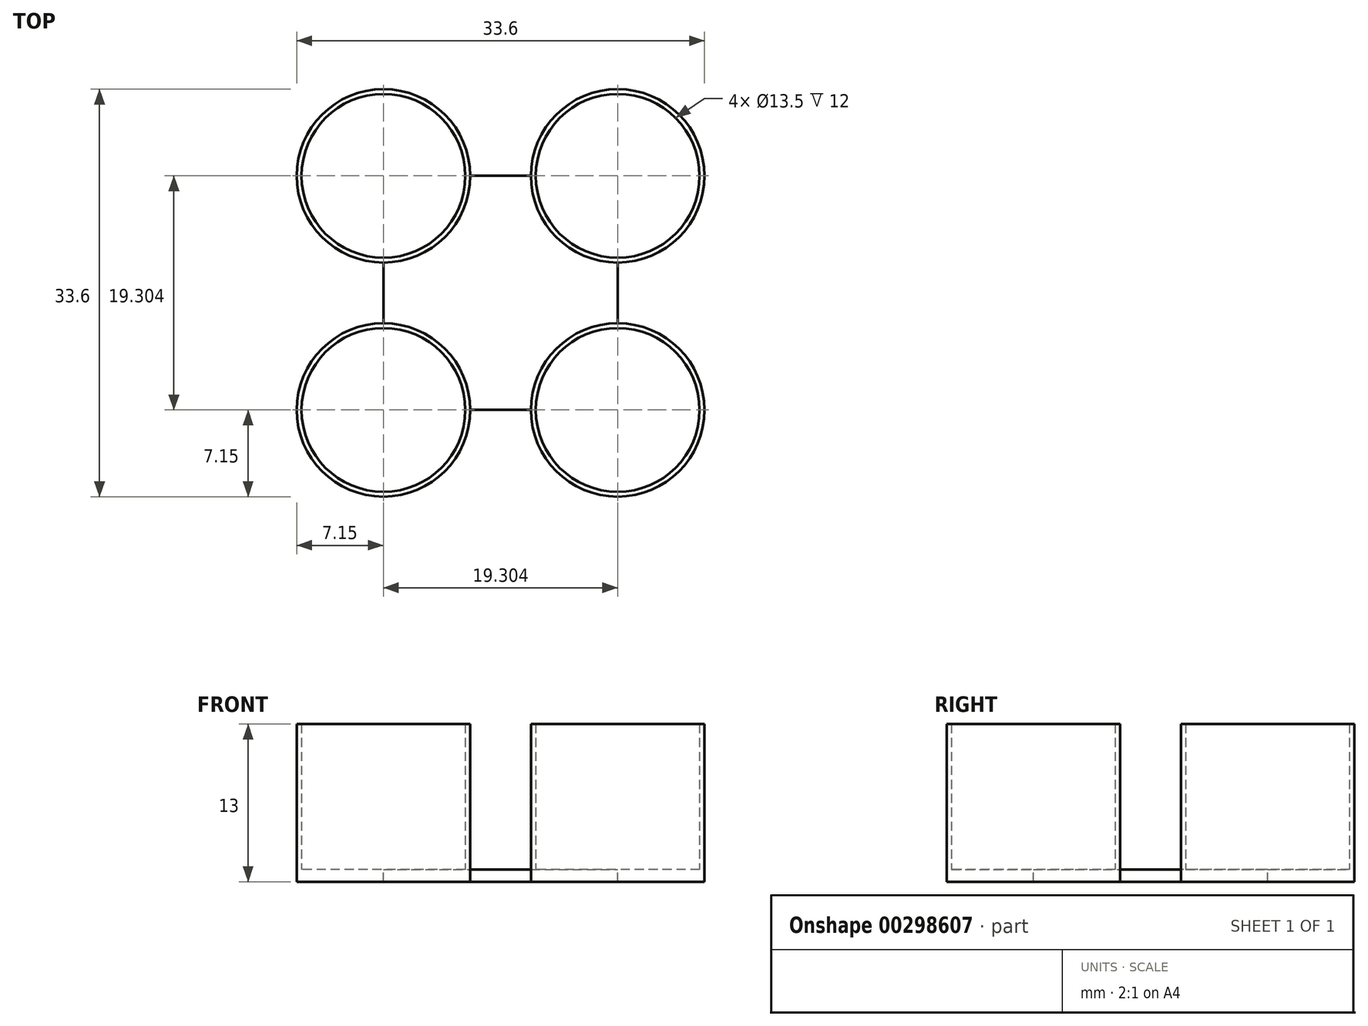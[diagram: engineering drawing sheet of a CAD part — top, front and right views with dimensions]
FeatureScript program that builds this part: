
annotation { "Feature Type Name" : "Feature", "Feature Type Description" : "" }
export const myFeature = defineFeature(function(context is Context, id is Id, definition is map)
    precondition{}
    {
        {
            var Q0;
            Q0=qCreatedBy(makeId("Top.planeOp"),FACE);
            var sketch = newSketch(context, id + "F0", { "sketchPlane" : qUnion([Q0])});
            skCircle(sketch, "E0", {"center": v(0, 0) * mm, "radius": 6.75 * mm});
            skCircle(sketch, "E1", {"center": v(0, 0) * mm, "radius": 7.15 * mm});
            skCircle(sketch, "E2.0.1.0", {"center": v(0, 19.3) * mm, "radius": 7.15 * mm});
            skCircle(sketch, "E2.0.1.1", {"center": v(0, 19.3) * mm, "radius": 6.75 * mm});
            skCircle(sketch, "E2.1.0.0", {"center": v(19.3, 0) * mm, "radius": 7.15 * mm});
            skCircle(sketch, "E2.1.0.1", {"center": v(19.3, 0) * mm, "radius": 6.75 * mm});
            skCircle(sketch, "E2.1.1.0", {"center": v(19.3, 19.3) * mm, "radius": 7.15 * mm});
            skCircle(sketch, "E2.1.1.1", {"center": v(19.3, 19.3) * mm, "radius": 6.75 * mm});
            skLineSegment(sketch, "E2.direction1", {"start": v(0, 0) * mm, "end": v(19.3, 0) * mm, "construction": true});
            skLineSegment(sketch, "E2.direction2", {"start": v(0, 0) * mm, "end": v(0, 19.3) * mm, "construction": true});
            skLineSegment(sketch, "E3", {"start": v(19.3, 19.3) * mm, "end": v(19.3, 0) * mm});
            skLineSegment(sketch, "E4", {"start": v(0, 19.3) * mm, "end": v(0, 0) * mm});
            skLineSegment(sketch, "E5", {"start": v(19.3, 19.3) * mm, "end": v(0, 19.3) * mm});
            skLineSegment(sketch, "E6", {"start": v(19.3, 0) * mm, "end": v(0, 0) * mm});
            skSolve(sketch);
        }
        {
            var Q0;
            {var subQ5=sQuery(id+"F0.wireOp",EDGE,"E4");var subQ13=sQuery(id+"F0.wireOp",EDGE,"E1");var subQ14=makeQuery(id+"F0.imprint","INTERSECT",VERTEX,{"derivedFrom":[subQ13,subQ5]});Q0=makeQuery(id+"F0.imprint","IMPRINT",FACE,{"disambiguationData":[TD([[makeQuery(id+"F0.imprint","IMPRINT",EDGE,{"disambiguationData":[TD([[subQ14,1.0]])],"derivedFrom":subQ13}),-1.0]])]});}
            var Q1;
            {var subQ0=sQuery(id+"F0.wireOp",EDGE,"E4");var subQ1=sQuery(id+"F0.wireOp",EDGE,"E2.0.1.0");var subQ2=makeQuery(id+"F0.imprint","INTERSECT",VERTEX,{"derivedFrom":[subQ1,subQ0]});Q1=makeQuery(id+"F0.imprint","IMPRINT",FACE,{"disambiguationData":[TD([[makeQuery(id+"F0.imprint","IMPRINT",EDGE,{"disambiguationData":[TD([[subQ2,-1.0]])],"derivedFrom":subQ1}),1.0]])]});}
            var Q2;
            {var subQ0=sQuery(id+"F0.wireOp",EDGE,"E3");var subQ1=sQuery(id+"F0.wireOp",EDGE,"E2.1.0.0");var subQ2=makeQuery(id+"F0.imprint","INTERSECT",VERTEX,{"derivedFrom":[subQ1,subQ0]});Q2=makeQuery(id+"F0.imprint","IMPRINT",FACE,{"disambiguationData":[TD([[makeQuery(id+"F0.imprint","IMPRINT",EDGE,{"disambiguationData":[TD([[subQ2,-1.0]])],"derivedFrom":subQ1}),1.0]])]});}
            var Q3;
            {var subQ0=sQuery(id+"F0.wireOp",EDGE,"E4");var subQ1=sQuery(id+"F0.wireOp",EDGE,"E0");var subQ2=makeQuery(id+"F0.imprint","INTERSECT",VERTEX,{"derivedFrom":[subQ1,subQ0]});Q3=makeQuery(id+"F0.imprint","IMPRINT",FACE,{"disambiguationData":[TD([[makeQuery(id+"F0.imprint","IMPRINT",EDGE,{"disambiguationData":[TD([[subQ2,1.0]])],"derivedFrom":subQ1}),1.0]])]});}
            var Q4;
            {var subQ0=sQuery(id+"F0.wireOp",EDGE,"E4");var subQ1=sQuery(id+"F0.wireOp",EDGE,"E0");var subQ2=makeQuery(id+"F0.imprint","INTERSECT",VERTEX,{"derivedFrom":[subQ1,subQ0]});Q4=makeQuery(id+"F0.imprint","IMPRINT",FACE,{"disambiguationData":[TD([[makeQuery(id+"F0.imprint","IMPRINT",EDGE,{"disambiguationData":[TD([[subQ2,-1.0]])],"derivedFrom":subQ1}),-1.0]])]});}
            var Q5;
            {var subQ0=sQuery(id+"F0.wireOp",EDGE,"E4");var subQ1=sQuery(id+"F0.wireOp",EDGE,"E0");var subQ2=makeQuery(id+"F0.imprint","INTERSECT",VERTEX,{"derivedFrom":[subQ1,subQ0]});Q5=makeQuery(id+"F0.imprint","IMPRINT",FACE,{"disambiguationData":[TD([[makeQuery(id+"F0.imprint","IMPRINT",EDGE,{"disambiguationData":[TD([[subQ2,-1.0]])],"derivedFrom":subQ1}),1.0]])]});}
            var Q6;
            {var subQ0=sQuery(id+"F0.wireOp",EDGE,"E4");var subQ1=sQuery(id+"F0.wireOp",EDGE,"E2.0.1.0");var subQ2=makeQuery(id+"F0.imprint","INTERSECT",VERTEX,{"derivedFrom":[subQ1,subQ0]});Q6=makeQuery(id+"F0.imprint","IMPRINT",FACE,{"disambiguationData":[TD([[makeQuery(id+"F0.imprint","IMPRINT",EDGE,{"disambiguationData":[TD([[subQ2,1.0]])],"derivedFrom":subQ1}),1.0]])]});}
            var Q7;
            {var subQ0=sQuery(id+"F0.wireOp",EDGE,"E4");var subQ1=sQuery(id+"F0.wireOp",EDGE,"E2.0.1.1");var subQ2=makeQuery(id+"F0.imprint","INTERSECT",VERTEX,{"derivedFrom":[subQ1,subQ0]});Q7=makeQuery(id+"F0.imprint","IMPRINT",FACE,{"disambiguationData":[TD([[makeQuery(id+"F0.imprint","IMPRINT",EDGE,{"disambiguationData":[TD([[subQ2,1.0]])],"derivedFrom":subQ1}),1.0]])]});}
            var Q8;
            {var subQ0=sQuery(id+"F0.wireOp",EDGE,"E4");var subQ1=sQuery(id+"F0.wireOp",EDGE,"E2.0.1.1");var subQ2=makeQuery(id+"F0.imprint","INTERSECT",VERTEX,{"derivedFrom":[subQ1,subQ0]});Q8=makeQuery(id+"F0.imprint","IMPRINT",FACE,{"disambiguationData":[TD([[makeQuery(id+"F0.imprint","IMPRINT",EDGE,{"disambiguationData":[TD([[subQ2,-1.0]])],"derivedFrom":subQ1}),1.0]])]});}
            var Q9;
            {var subQ0=sQuery(id+"F0.wireOp",EDGE,"E3");var subQ1=sQuery(id+"F0.wireOp",EDGE,"E2.1.1.0");var subQ2=makeQuery(id+"F0.imprint","INTERSECT",VERTEX,{"derivedFrom":[subQ1,subQ0]});Q9=makeQuery(id+"F0.imprint","IMPRINT",FACE,{"disambiguationData":[TD([[makeQuery(id+"F0.imprint","IMPRINT",EDGE,{"disambiguationData":[TD([[subQ2,1.0]])],"derivedFrom":subQ1}),1.0]])]});}
            var Q10;
            {var subQ0=sQuery(id+"F0.wireOp",EDGE,"E3");var subQ1=sQuery(id+"F0.wireOp",EDGE,"E2.1.0.0");var subQ2=makeQuery(id+"F0.imprint","INTERSECT",VERTEX,{"derivedFrom":[subQ1,subQ0]});Q10=makeQuery(id+"F0.imprint","IMPRINT",FACE,{"disambiguationData":[TD([[makeQuery(id+"F0.imprint","IMPRINT",EDGE,{"disambiguationData":[TD([[subQ2,1.0]])],"derivedFrom":subQ1}),1.0]])]});}
            var Q11;
            {var subQ0=sQuery(id+"F0.wireOp",EDGE,"E3");var subQ1=sQuery(id+"F0.wireOp",EDGE,"E2.1.0.1");var subQ2=makeQuery(id+"F0.imprint","INTERSECT",VERTEX,{"derivedFrom":[subQ1,subQ0]});Q11=makeQuery(id+"F0.imprint","IMPRINT",FACE,{"disambiguationData":[TD([[makeQuery(id+"F0.imprint","IMPRINT",EDGE,{"disambiguationData":[TD([[subQ2,-1.0]])],"derivedFrom":subQ1}),1.0]])]});}
            var Q12;
            {var subQ0=sQuery(id+"F0.wireOp",EDGE,"E3");var subQ1=sQuery(id+"F0.wireOp",EDGE,"E2.1.0.1");var subQ2=makeQuery(id+"F0.imprint","INTERSECT",VERTEX,{"derivedFrom":[subQ1,subQ0]});Q12=makeQuery(id+"F0.imprint","IMPRINT",FACE,{"disambiguationData":[TD([[makeQuery(id+"F0.imprint","IMPRINT",EDGE,{"disambiguationData":[TD([[subQ2,1.0]])],"derivedFrom":subQ1}),1.0]])]});}
            var Q13;
            {var subQ0=sQuery(id+"F0.wireOp",EDGE,"E3");var subQ1=sQuery(id+"F0.wireOp",EDGE,"E2.1.1.0");var subQ2=makeQuery(id+"F0.imprint","INTERSECT",VERTEX,{"derivedFrom":[subQ1,subQ0]});Q13=makeQuery(id+"F0.imprint","IMPRINT",FACE,{"disambiguationData":[TD([[makeQuery(id+"F0.imprint","IMPRINT",EDGE,{"disambiguationData":[TD([[subQ2,-1.0]])],"derivedFrom":subQ1}),1.0]])]});}
            var Q14;
            {var subQ0=sQuery(id+"F0.wireOp",EDGE,"E3");var subQ1=sQuery(id+"F0.wireOp",EDGE,"E2.1.1.1");var subQ2=makeQuery(id+"F0.imprint","INTERSECT",VERTEX,{"derivedFrom":[subQ1,subQ0]});Q14=makeQuery(id+"F0.imprint","IMPRINT",FACE,{"disambiguationData":[TD([[makeQuery(id+"F0.imprint","IMPRINT",EDGE,{"disambiguationData":[TD([[subQ2,1.0]])],"derivedFrom":subQ1}),1.0]])]});}
            var Q15;
            {var subQ0=sQuery(id+"F0.wireOp",EDGE,"E3");var subQ1=sQuery(id+"F0.wireOp",EDGE,"E2.1.1.1");var subQ2=makeQuery(id+"F0.imprint","INTERSECT",VERTEX,{"derivedFrom":[subQ1,subQ0]});Q15=makeQuery(id+"F0.imprint","IMPRINT",FACE,{"disambiguationData":[TD([[makeQuery(id+"F0.imprint","IMPRINT",EDGE,{"disambiguationData":[TD([[subQ2,-1.0]])],"derivedFrom":subQ1}),1.0]])]});}
            var Q16;
            {var subQ0=sQuery(id+"F0.wireOp",EDGE,"E4");var subQ1=sQuery(id+"F0.wireOp",EDGE,"E0");var subQ2=makeQuery(id+"F0.imprint","INTERSECT",VERTEX,{"derivedFrom":[subQ1,subQ0]});Q16=makeQuery(id+"F0.imprint","IMPRINT",FACE,{"disambiguationData":[TD([[makeQuery(id+"F0.imprint","IMPRINT",EDGE,{"disambiguationData":[TD([[subQ2,1.0]])],"derivedFrom":subQ1}),-1.0]])]});}
            var Q17;
            Q17=sQuery(id+"F0.wireOp",EDGE,"E2.1.0.0");
            var Q18;
            Q18=sQuery(id+"F0.wireOp",EDGE,"E2.0.1.1");
            var Q19;
            Q19=sQuery(id+"F0.wireOp",EDGE,"E2.1.0.1");
            var Q20;
            Q20=sQuery(id+"F0.wireOp",EDGE,"E0");
            var Q21;
            Q21=sQuery(id+"F0.wireOp",EDGE,"E2.1.1.0");
            var Q22;
            Q22=sQuery(id+"F0.wireOp",EDGE,"E2.1.1.1");
            var Q23;
            Q23=sQuery(id+"F0.wireOp",EDGE,"E3");
            var Q24;
            Q24=sQuery(id+"F0.wireOp",EDGE,"E2.0.1.0");
            var Q25;
            Q25=sQuery(id+"F0.wireOp",EDGE,"E1");
            var Q26;
            Q26=sQuery(id+"F0.wireOp",EDGE,"E5");
            var Q27;
            Q27=sQuery(id+"F0.wireOp",EDGE,"E4");
            var Q28;
            Q28=sQuery(id+"F0.wireOp",EDGE,"E6");
            extrude(context, id + "F1", {"entities" : qUnion([Q0, Q1, Q2, Q3, Q4, Q5, Q6, Q7, Q8, Q9, Q10, Q11, Q12, Q13, Q14, Q15, Q16]), "surfaceEntities" : qUnion([Q17, Q18, Q19, Q20, Q21, Q22, Q23, Q24, Q25, Q26, Q27, Q28]), "oppositeDirection" : true, "depth" : 1 * mm});
        }
        {
            var Q0;
            {var subQ0=sQuery(id+"F0.wireOp",EDGE,"E4");var subQ1=sQuery(id+"F0.wireOp",EDGE,"E2.0.1.0");var subQ2=makeQuery(id+"F0.imprint","INTERSECT",VERTEX,{"derivedFrom":[subQ1,subQ0]});Q0=makeQuery(id+"F0.imprint","IMPRINT",FACE,{"disambiguationData":[TD([[makeQuery(id+"F0.imprint","IMPRINT",EDGE,{"disambiguationData":[TD([[subQ2,1.0]])],"derivedFrom":subQ1}),1.0]])]});}
            var Q1;
            {var subQ0=sQuery(id+"F0.wireOp",EDGE,"E4");var subQ1=sQuery(id+"F0.wireOp",EDGE,"E2.0.1.0");var subQ2=makeQuery(id+"F0.imprint","INTERSECT",VERTEX,{"derivedFrom":[subQ1,subQ0]});Q1=makeQuery(id+"F0.imprint","IMPRINT",FACE,{"disambiguationData":[TD([[makeQuery(id+"F0.imprint","IMPRINT",EDGE,{"disambiguationData":[TD([[subQ2,-1.0]])],"derivedFrom":subQ1}),1.0]])]});}
            var Q2;
            {var subQ0=sQuery(id+"F0.wireOp",EDGE,"E4");var subQ1=sQuery(id+"F0.wireOp",EDGE,"E0");var subQ2=makeQuery(id+"F0.imprint","INTERSECT",VERTEX,{"derivedFrom":[subQ1,subQ0]});Q2=makeQuery(id+"F0.imprint","IMPRINT",FACE,{"disambiguationData":[TD([[makeQuery(id+"F0.imprint","IMPRINT",EDGE,{"disambiguationData":[TD([[subQ2,-1.0]])],"derivedFrom":subQ1}),-1.0]])]});}
            var Q3;
            {var subQ0=sQuery(id+"F0.wireOp",EDGE,"E4");var subQ1=sQuery(id+"F0.wireOp",EDGE,"E0");var subQ2=makeQuery(id+"F0.imprint","INTERSECT",VERTEX,{"derivedFrom":[subQ1,subQ0]});Q3=makeQuery(id+"F0.imprint","IMPRINT",FACE,{"disambiguationData":[TD([[makeQuery(id+"F0.imprint","IMPRINT",EDGE,{"disambiguationData":[TD([[subQ2,1.0]])],"derivedFrom":subQ1}),-1.0]])]});}
            var Q4;
            {var subQ0=sQuery(id+"F0.wireOp",EDGE,"E3");var subQ1=sQuery(id+"F0.wireOp",EDGE,"E2.1.0.0");var subQ2=makeQuery(id+"F0.imprint","INTERSECT",VERTEX,{"derivedFrom":[subQ1,subQ0]});Q4=makeQuery(id+"F0.imprint","IMPRINT",FACE,{"disambiguationData":[TD([[makeQuery(id+"F0.imprint","IMPRINT",EDGE,{"disambiguationData":[TD([[subQ2,-1.0]])],"derivedFrom":subQ1}),1.0]])]});}
            var Q5;
            {var subQ0=sQuery(id+"F0.wireOp",EDGE,"E3");var subQ1=sQuery(id+"F0.wireOp",EDGE,"E2.1.0.0");var subQ2=makeQuery(id+"F0.imprint","INTERSECT",VERTEX,{"derivedFrom":[subQ1,subQ0]});Q5=makeQuery(id+"F0.imprint","IMPRINT",FACE,{"disambiguationData":[TD([[makeQuery(id+"F0.imprint","IMPRINT",EDGE,{"disambiguationData":[TD([[subQ2,1.0]])],"derivedFrom":subQ1}),1.0]])]});}
            var Q6;
            {var subQ0=sQuery(id+"F0.wireOp",EDGE,"E3");var subQ1=sQuery(id+"F0.wireOp",EDGE,"E2.1.1.0");var subQ2=makeQuery(id+"F0.imprint","INTERSECT",VERTEX,{"derivedFrom":[subQ1,subQ0]});Q6=makeQuery(id+"F0.imprint","IMPRINT",FACE,{"disambiguationData":[TD([[makeQuery(id+"F0.imprint","IMPRINT",EDGE,{"disambiguationData":[TD([[subQ2,1.0]])],"derivedFrom":subQ1}),1.0]])]});}
            var Q7;
            {var subQ0=sQuery(id+"F0.wireOp",EDGE,"E3");var subQ1=sQuery(id+"F0.wireOp",EDGE,"E2.1.1.0");var subQ2=makeQuery(id+"F0.imprint","INTERSECT",VERTEX,{"derivedFrom":[subQ1,subQ0]});Q7=makeQuery(id+"F0.imprint","IMPRINT",FACE,{"disambiguationData":[TD([[makeQuery(id+"F0.imprint","IMPRINT",EDGE,{"disambiguationData":[TD([[subQ2,-1.0]])],"derivedFrom":subQ1}),1.0]])]});}
            extrude(context, id + "F2", {"entities" : qUnion([Q0, Q1, Q2, Q3, Q4, Q5, Q6, Q7]), "operationType" : NewBodyOperationType.ADD, "depth" : 12 * mm});
        }
    });
